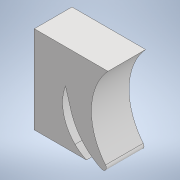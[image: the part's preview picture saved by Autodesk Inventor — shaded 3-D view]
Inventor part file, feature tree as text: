
AUTODESK INVENTOR PART (.ipt)
format: ipt  version: 2022 (Build 260153000, 153)  size: 115,200 bytes
history: native  units: in
note: dims shown in document units (in); Inventor stores cm internally (conversion verified against a paired STEP export)
features: sketch x2, sheet_metal_op x1, other x1
ambient origin geometry x8: Origin, YZ Plane, XZ Plane, XY Plane, X Axis, Y Axis, Z Axis, Center Point
bodies: Solid1 (feature_tree)
feature tree (4):
  sketch  "Sketch1"  dims[d0=0.12in]
  sheet_metal_op  "Face1"
  sketch  "Sketch2"
  other  "Plate1"
